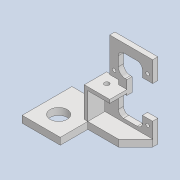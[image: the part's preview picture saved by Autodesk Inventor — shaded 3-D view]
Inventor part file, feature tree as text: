
AUTODESK INVENTOR PART (.ipt)
format: ipt  version: 2020 (Build 240168000, 168)  size: 349,696 bytes
history: native  units: mm
features: extrude x12, sketch x12, projected_geometry x12, reference x7, other x6, thicken_offset x4, fillet x2, chamfer x2
ambient origin geometry x8: Origin, YZ Plane, XZ Plane, XY Plane, X Axis, Y Axis, Z Axis, Center Point
bodies: Solid1 (feature_tree)
feature tree (57):
  extrude  "Extrusion1"  Depth=15.0mm
  extrude  "Extrusion2"  Depth=2.0mm
  extrude  "Extrusion3"  Depth=8.0mm
  extrude  "Extrusion4"  Depth=1.0mm
  extrude  "Extrusion5"  Depth=2.0mm
  extrude  "Extrusion6"  Depth=5.0mm
  fillet  "Fillet1"  Radius=3.85mm
  thicken_offset  "Thicken1"
  extrude  "Extrusion7"  Depth=8.0mm
  fillet  "Fillet3"  Radius=8.0mm
  extrude  "Extrusion8"  Depth=10.0mm TaperAngle=0.0deg
  thicken_offset  "Thicken2"
  thicken_offset  "Thicken3"
  extrude  "Extrusion9"  Depth=5.0mm
  extrude  "Extrusion10"  Depth=10.0mm TaperAngle=0.0deg
  extrude  "Extrusion11"  Depth=4.0mm
  extrude  "Extrusion12"  Depth=5.0mm
  chamfer  "Chamfer1"  Distance=9.0mm
  thicken_offset  "Thicken4"
  chamfer  "Chamfer2"  Distance=25.0mm
  sketch  "Sketch1"  dims[d0=5.0mm d1=15.0mm]
  reference  "Reference1"
  reference  "Reference2"
  sketch  "Sketch2"  dims[d2=3.0mm d3=0.0mm d4=2.0mm]
  projected_geometry  "Projected Loop1"
  sketch  "Sketch3"  dims[d5=6.0mm d6=8.0mm]
  projected_geometry  "Projected Loop2"
  sketch  "Sketch4"  dims[d7=3.0mm d8=0.0mm d9=1.0mm]
  reference  "Reference3"
  projected_geometry  "Projected Loop3"
  projected_geometry  "Projected Loop4"
  projected_geometry  "Projected Loop5"
  sketch  "Sketch5"  dims[d10=10.0mm d11=2.0mm]
  reference  "Reference4"
  sketch  "Sketch6"  dims[d12=10.0mm d13=0.0mm d14=5.0mm d15=3.85mm]
  projected_geometry  "Projected Loop6"
  projected_geometry  "Projected Loop7"
  sketch  "Sketch7"  dims[d16=3.0mm d17=8.0mm d18=8.0mm]
  reference  "Reference5"
  reference  "Reference6"
  sketch  "Sketch8"  dims[d19=11.9mm d20=10.0mm d21=0.0mm]
  projected_geometry  "Projected Loop8"
  sketch  "Sketch9"  dims[d22=5.0mm d23=3.85mm]
  projected_geometry  "Projected Loop9"
  sketch  "Sketch10"  dims[d24=2.8mm d25=10.0mm d26=0.0mm]
  projected_geometry  "Projected Loop10"
  reference  "Reference7"
  sketch  "Sketch11"  dims[d27=2.5mm d28=0.0mm d29=4.0mm]
  projected_geometry  "Projected Loop11"
  sketch  "Sketch12"  dims[d31=1.1mm d32=1.0mm d33=5.0mm d34=9.0mm d35=25.0mm d36=5.0mm d37=6.0mm d38=7.0mm d39=5.0mm d40=9.0mm d41=25.0mm d42=5.0mm d43=6.0mm d44=7.0mm d45=3.0mm d46=0.0mm d47=3.0mm d48=4.0mm d49=50.0mm d50=3.0mm d51=30.0mm d52=0.0mm d53=3.0mm d54=3.0mm d55=1.0mm d56=1.0mm d57=30.0mm d58=0.0mm d59=16.0mm d60=12.0mm d61=10.0mm d62=30.0mm d63=0.0mm d64=2.0mm d65=17.5mm d66=30.0mm d67=0.0mm d68=30.0mm d69=0.0mm d70=10.0mm d71=2.0mm d72=45.0deg d73=4.0mm d74=4.0mm d75=10.0mm d76=2.0mm d77=45.0deg]
  projected_geometry  "Projected Loop12"
  parser-record x1  (decoder bookkeeping rows leaked as tree rows — omitted from the tree; the rows remain in map.json)
  other  "tip_3_n_base_ass.iam"
  other  "ext_pin_shell_2:1"
  other  "bl_tube_ass_2:1"
  other  "bl_tube_hn_1:1"
  other  "bearing_3_6_2:5"
note: 1 file-system path scrubbed to <path> (originals preserved in map.json)
